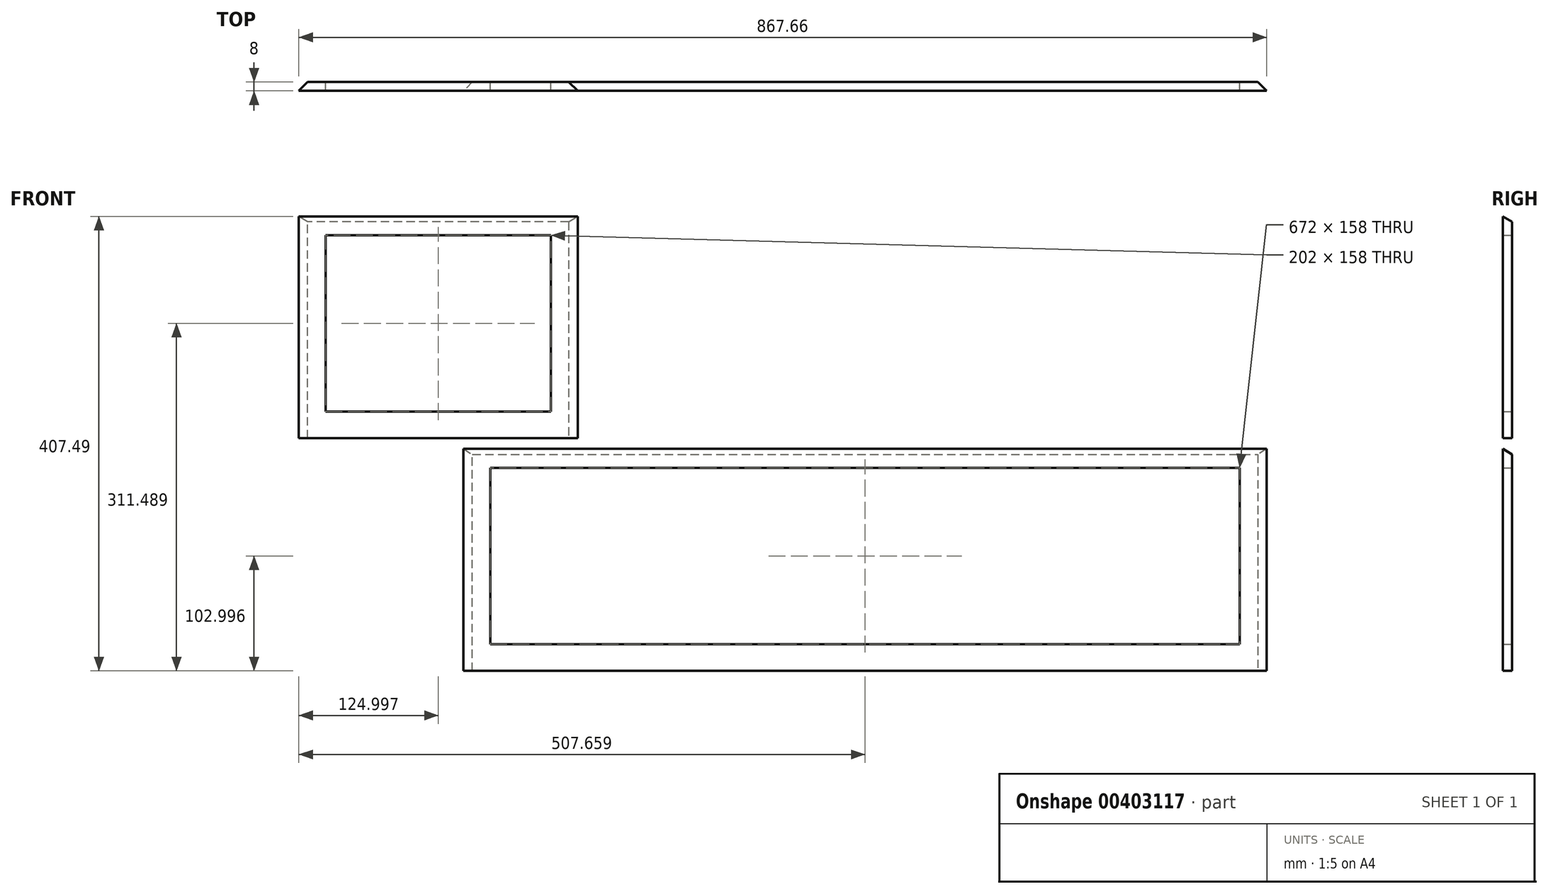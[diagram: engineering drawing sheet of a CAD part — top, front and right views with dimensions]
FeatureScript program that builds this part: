
annotation { "Feature Type Name" : "Feature", "Feature Type Description" : "" }
export const myFeature = defineFeature(function(context is Context, id is Id, definition is map)
    precondition{}
    {
        {
            var Q0;
            Q0=qCreatedBy(makeId("Front.planeOp"),FACE);
            var sketch = newSketch(context, id + "F0", { "sketchPlane" : qUnion([Q0])});
            skLineSegment(sketch, "E0.bottom", {"start": v(-345.91, 117.95) * mm, "end": v(374.09, 117.95) * mm});
            skLineSegment(sketch, "E0.top", {"start": v(-345.91, -76.05) * mm, "end": v(374.09, -76.05) * mm});
            skLineSegment(sketch, "E0.left", {"start": v(-345.91, 117.95) * mm, "end": v(-345.91, -76.05) * mm});
            skLineSegment(sketch, "E0.right", {"start": v(374.09, 117.95) * mm, "end": v(374.09, -76.05) * mm});
            skLineSegment(sketch, "E1.bottom", {"start": v(-345.91, 117.95) * mm, "end": v(-321.91, 117.95) * mm});
            skLineSegment(sketch, "E1.top", {"start": v(-345.91, 105.95) * mm, "end": v(-321.91, 105.95) * mm});
            skLineSegment(sketch, "E1.left", {"start": v(-345.91, 117.95) * mm, "end": v(-345.91, 105.95) * mm});
            skLineSegment(sketch, "E1.right", {"start": v(-321.91, 117.95) * mm, "end": v(-321.91, 105.95) * mm});
            skLineSegment(sketch, "E2.bottom", {"start": v(374.09, 117.95) * mm, "end": v(350.09, 117.95) * mm});
            skLineSegment(sketch, "E2.top", {"start": v(374.09, 105.95) * mm, "end": v(350.09, 105.95) * mm});
            skLineSegment(sketch, "E2.left", {"start": v(374.09, 117.95) * mm, "end": v(374.09, 105.95) * mm});
            skLineSegment(sketch, "E2.right", {"start": v(350.09, 117.95) * mm, "end": v(350.09, 105.95) * mm});
            skLineSegment(sketch, "E3", {"start": v(350.09, 105.95) * mm, "end": v(-321.91, 105.95) * mm});
            skLineSegment(sketch, "E4.bottom", {"start": v(-345.91, -76.05) * mm, "end": v(-321.91, -76.05) * mm});
            skLineSegment(sketch, "E4.top", {"start": v(-345.91, -52.05) * mm, "end": v(-321.91, -52.05) * mm});
            skLineSegment(sketch, "E4.left", {"start": v(-345.91, -76.05) * mm, "end": v(-345.91, -52.05) * mm});
            skLineSegment(sketch, "E4.right", {"start": v(-321.91, -76.05) * mm, "end": v(-321.91, -52.05) * mm});
            skLineSegment(sketch, "E5.bottom", {"start": v(374.09, -76.05) * mm, "end": v(350.09, -76.05) * mm});
            skLineSegment(sketch, "E5.top", {"start": v(374.09, -52.05) * mm, "end": v(350.09, -52.05) * mm});
            skLineSegment(sketch, "E5.left", {"start": v(374.09, -76.05) * mm, "end": v(374.09, -52.05) * mm});
            skLineSegment(sketch, "E5.right", {"start": v(350.09, -76.05) * mm, "end": v(350.09, -52.05) * mm});
            skLineSegment(sketch, "E6", {"start": v(-321.91, 105.95) * mm, "end": v(-321.91, -52.05) * mm});
            skLineSegment(sketch, "E7", {"start": v(-321.91, -52.05) * mm, "end": v(350.09, -52.05) * mm});
            skLineSegment(sketch, "E8", {"start": v(350.09, -52.05) * mm, "end": v(350.09, 105.95) * mm});
            skSolve(sketch);
        }
        {
            var Q0;
            Q0=makeQuery(id+"F0.imprint","IMPRINT",FACE,{"disambiguationData":[TD([[makeQuery(id+"F0.imprint","IMPRINT",EDGE,{"derivedFrom":sQuery(id+"F0.wireOp",EDGE,"E1.bottom")}),-1.0]])]});
            var Q1;
            Q1=makeQuery(id+"F0.imprint","IMPRINT",FACE,{"disambiguationData":[TD([[makeQuery(id+"F0.imprint","IMPRINT",EDGE,{"derivedFrom":sQuery(id+"F0.wireOp",EDGE,"E0.bottom")}),-1.0]])]});
            var Q2;
            Q2=makeQuery(id+"F0.imprint","IMPRINT",FACE,{"disambiguationData":[TD([[makeQuery(id+"F0.imprint","IMPRINT",EDGE,{"derivedFrom":sQuery(id+"F0.wireOp",EDGE,"E0.left")}),1.0]])]});
            var Q3;
            Q3=makeQuery(id+"F0.imprint","IMPRINT",FACE,{"disambiguationData":[TD([[makeQuery(id+"F0.imprint","IMPRINT",EDGE,{"derivedFrom":sQuery(id+"F0.wireOp",EDGE,"E4.bottom")}),1.0]])]});
            var Q4;
            Q4=makeQuery(id+"F0.imprint","IMPRINT",FACE,{"disambiguationData":[TD([[makeQuery(id+"F0.imprint","IMPRINT",EDGE,{"derivedFrom":sQuery(id+"F0.wireOp",EDGE,"E0.top")}),1.0]])]});
            var Q5;
            Q5=makeQuery(id+"F0.imprint","IMPRINT",FACE,{"disambiguationData":[TD([[makeQuery(id+"F0.imprint","IMPRINT",EDGE,{"derivedFrom":sQuery(id+"F0.wireOp",EDGE,"E2.bottom")}),1.0]])]});
            var Q6;
            Q6=makeQuery(id+"F0.imprint","IMPRINT",FACE,{"disambiguationData":[TD([[makeQuery(id+"F0.imprint","IMPRINT",EDGE,{"derivedFrom":sQuery(id+"F0.wireOp",EDGE,"E0.right")}),-1.0]])]});
            var Q7;
            Q7=makeQuery(id+"F0.imprint","IMPRINT",FACE,{"disambiguationData":[TD([[makeQuery(id+"F0.imprint","IMPRINT",EDGE,{"derivedFrom":sQuery(id+"F0.wireOp",EDGE,"E5.bottom")}),-1.0]])]});
            extrude(context, id + "F1", {"entities" : qUnion([Q0, Q1, Q2, Q3, Q4, Q5, Q6, Q7]), "depth" : 8 * mm});
        }
        {
            var Q0;
            Q0=makeQuery(id+"F1.opExtrude","SWEPT_FACE",FACE,{"disambiguationData":[OSD([sQuery(id+"F0.wireOp",EDGE,"E0.right"),sQuery(id+"F0.wireOp",EDGE,"E2.left"),sQuery(id+"F0.wireOp",EDGE,"E5.left")])]});
            var sketch = newSketch(context, id + "F2", { "sketchPlane" : qUnion([Q0])});
            skLineSegment(sketch, "E9", {"start": v(-8, 117.95) * mm, "end": v(-8, 122.95) * mm});
            skLineSegment(sketch, "E10", {"start": v(-8, 122.95) * mm, "end": v(0, 117.95) * mm});
            skLineSegment(sketch, "E11", {"start": v(0, 117.95) * mm, "end": v(-8, 117.95) * mm});
            skSolve(sketch);
        }
        {
            var Q0;
            Q0=makeQuery(id+"F2.imprint","IMPRINT",FACE,{"disambiguationData":[TD([[makeQuery(id+"F2.imprint","IMPRINT",EDGE,{"derivedFrom":sQuery(id+"F2.wireOp",EDGE,"E9")}),-1.0]])]});
            extrude(context, id + "F3", {"entities" : qUnion([Q0]), "operationType" : NewBodyOperationType.ADD, "oppositeDirection" : true, "depth" : 720 * mm});
        }
        {
            var Q0;
            Q0=makeQuery(id+"F1.opExtrude","CAP_EDGE",EDGE,{"disambiguationData":[OSD([sQuery(id+"F0.wireOp",EDGE,"E0.right"),sQuery(id+"F0.wireOp",EDGE,"E2.left"),sQuery(id+"F0.wireOp",EDGE,"E5.left")])],"isStart":true});
            var Q1;
            Q1=makeQuery(id+"F1.opExtrude","CAP_EDGE",EDGE,{"disambiguationData":[OSD([sQuery(id+"F0.wireOp",EDGE,"E0.left"),sQuery(id+"F0.wireOp",EDGE,"E1.left"),sQuery(id+"F0.wireOp",EDGE,"E4.left")])],"isStart":true});
            chamfer(context, id + "F4", {"entities" : qUnion([Q0, Q1]), "width" : 8 * mm, "tangentPropagation" : true});
        }
        {
            var Q0;
            Q0=qCreatedBy(makeId("Front.planeOp"),FACE);
            var sketch = newSketch(context, id + "F5", { "sketchPlane" : qUnion([Q0])});
            skLineSegment(sketch, "E12.bottom", {"start": v(-243.57, 132.44) * mm, "end": v(-493.57, 132.44) * mm});
            skLineSegment(sketch, "E12.top", {"start": v(-243.57, 326.44) * mm, "end": v(-493.57, 326.44) * mm});
            skLineSegment(sketch, "E12.left", {"start": v(-243.57, 132.44) * mm, "end": v(-243.57, 326.44) * mm});
            skLineSegment(sketch, "E12.right", {"start": v(-493.57, 132.44) * mm, "end": v(-493.57, 326.44) * mm});
            skLineSegment(sketch, "E13.bottom", {"start": v(-243.57, 326.44) * mm, "end": v(-267.57, 326.44) * mm});
            skLineSegment(sketch, "E13.top", {"start": v(-243.57, 314.44) * mm, "end": v(-267.57, 314.44) * mm});
            skLineSegment(sketch, "E13.left", {"start": v(-243.57, 326.44) * mm, "end": v(-243.57, 314.44) * mm});
            skLineSegment(sketch, "E13.right", {"start": v(-267.57, 326.44) * mm, "end": v(-267.57, 314.44) * mm});
            skLineSegment(sketch, "E14.bottom", {"start": v(-493.57, 326.44) * mm, "end": v(-469.57, 326.44) * mm});
            skLineSegment(sketch, "E14.top", {"start": v(-493.57, 314.44) * mm, "end": v(-469.57, 314.44) * mm});
            skLineSegment(sketch, "E14.left", {"start": v(-493.57, 326.44) * mm, "end": v(-493.57, 314.44) * mm});
            skLineSegment(sketch, "E14.right", {"start": v(-469.57, 326.44) * mm, "end": v(-469.57, 314.44) * mm});
            skLineSegment(sketch, "E15.bottom", {"start": v(-243.57, 132.44) * mm, "end": v(-267.57, 132.44) * mm});
            skLineSegment(sketch, "E15.top", {"start": v(-243.57, 156.44) * mm, "end": v(-267.57, 156.44) * mm});
            skLineSegment(sketch, "E15.left", {"start": v(-243.57, 132.44) * mm, "end": v(-243.57, 156.44) * mm});
            skLineSegment(sketch, "E15.right", {"start": v(-267.57, 132.44) * mm, "end": v(-267.57, 156.44) * mm});
            skLineSegment(sketch, "E16.bottom", {"start": v(-493.57, 132.44) * mm, "end": v(-469.57, 132.44) * mm});
            skLineSegment(sketch, "E16.top", {"start": v(-493.57, 156.44) * mm, "end": v(-469.57, 156.44) * mm});
            skLineSegment(sketch, "E16.left", {"start": v(-493.57, 132.44) * mm, "end": v(-493.57, 156.44) * mm});
            skLineSegment(sketch, "E16.right", {"start": v(-469.57, 132.44) * mm, "end": v(-469.57, 156.44) * mm});
            skLineSegment(sketch, "E17", {"start": v(-267.57, 156.44) * mm, "end": v(-469.57, 156.44) * mm});
            skLineSegment(sketch, "E18", {"start": v(-267.57, 314.44) * mm, "end": v(-267.57, 156.44) * mm});
            skLineSegment(sketch, "E19", {"start": v(-469.57, 314.44) * mm, "end": v(-267.57, 314.44) * mm});
            skLineSegment(sketch, "E20", {"start": v(-469.57, 314.44) * mm, "end": v(-469.57, 156.44) * mm});
            skSolve(sketch);
        }
        {
            var Q0;
            Q0 = qSketchRegion(id + "F5", true);
            extrude(context, id + "F6", {"entities" : qUnion([Q0]), "depth" : 8 * mm});
        }
        {
            var Q0;
            Q0=makeQuery(id+"F6.opExtrude","SWEPT_FACE",FACE,{"disambiguationData":[OSD([sQuery(id+"F5.wireOp",EDGE,"E12.right"),sQuery(id+"F5.wireOp",EDGE,"E14.left"),sQuery(id+"F5.wireOp",EDGE,"E16.left")])]});
            var sketch = newSketch(context, id + "F7", { "sketchPlane" : qUnion([Q0])});
            skLineSegment(sketch, "E21", {"start": v(8, 326.44) * mm, "end": v(8, 331.44) * mm});
            skLineSegment(sketch, "E22", {"start": v(8, 331.44) * mm, "end": v(0, 326.44) * mm});
            skSolve(sketch);
        }
        {
            var Q0;
            Q0 = qSketchRegion(id + "F7", true);
            var Q1;
            Q1=makeQuery(id+"F7.imprint","IMPRINT",FACE,{"disambiguationData":[TD([[makeQuery(id+"F7.imprint","IMPRINT",EDGE,{"derivedFrom":sQuery(id+"F7.wireOp",EDGE,"E21")}),1.0]])]});
            extrude(context, id + "F8", {"entities" : qUnion([Q0, Q1]), "operationType" : NewBodyOperationType.ADD, "oppositeDirection" : true, "depth" : 250 * mm});
        }
        {
            var Q0;
            Q0=makeQuery(id+"F6.opExtrude","CAP_EDGE",EDGE,{"disambiguationData":[OSD([sQuery(id+"F5.wireOp",EDGE,"E12.right"),sQuery(id+"F5.wireOp",EDGE,"E14.left"),sQuery(id+"F5.wireOp",EDGE,"E16.left")])],"isStart":true});
            var Q1;
            Q1=makeQuery(id+"F6.opExtrude","CAP_EDGE",EDGE,{"disambiguationData":[OSD([sQuery(id+"F5.wireOp",EDGE,"E12.left"),sQuery(id+"F5.wireOp",EDGE,"E13.left"),sQuery(id+"F5.wireOp",EDGE,"E15.left")])],"isStart":true});
            chamfer(context, id + "F9", {"entities" : qUnion([Q0, Q1]), "width" : 8 * mm, "tangentPropagation" : true});
        }
    });
